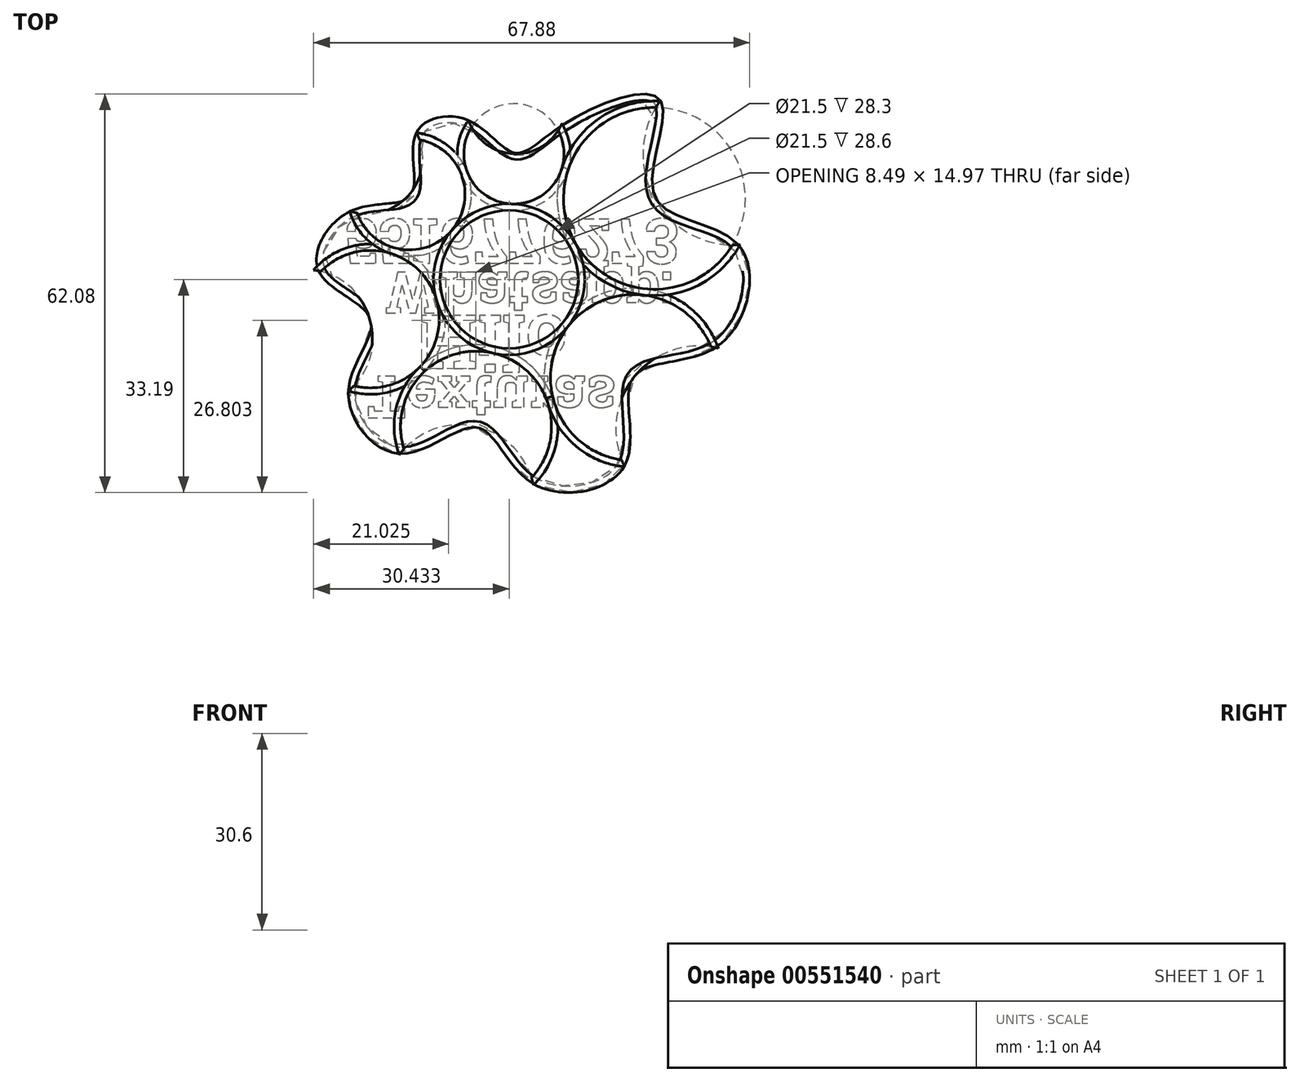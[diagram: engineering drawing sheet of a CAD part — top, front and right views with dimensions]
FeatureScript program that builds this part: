
annotation { "Feature Type Name" : "Feature", "Feature Type Description" : "" }
export const myFeature = defineFeature(function(context is Context, id is Id, definition is map)
    precondition{}
    {
        {
            var Q0;
            Q0=qCreatedBy(makeId("Top.planeOp"),FACE);
            var sketch = newSketch(context, id + "F0", { "sketchPlane" : qUnion([Q0])});
            skCircle(sketch, "E0", {"center": v(0, 0) * mm, "radius": 10.75 * mm});
            skCircle(sketch, "E1", {"center": v(14.53, -21.44) * mm, "radius": 14.15 * mm});
            skCircle(sketch, "E2", {"center": v(-13.56, -20.65) * mm, "radius": 12.95 * mm});
            skCircle(sketch, "E3", {"center": v(-23.3, 3.14) * mm, "radius": 11.75 * mm});
            skCircle(sketch, "E4", {"center": v(-8.05, 20.96) * mm, "radius": 10.7 * mm});
            skCircle(sketch, "E5", {"center": v(11.83, 16.62) * mm, "radius": 8.65 * mm});
            skCircle(sketch, "E6", {"center": v(19.53, 0.96) * mm, "radius": 7.8 * mm});
            skCircle(sketch, "E7", {"center": v(0, 0) * mm, "radius": 19.4 * mm});
            skLineSegment(sketch, "E8", {"start": v(0, 0) * mm, "end": v(14.53, -21.44) * mm, "construction": true});
            skLineSegment(sketch, "E9", {"start": v(0, 0) * mm, "end": v(19.53, 0.96) * mm, "construction": true});
            skLineSegment(sketch, "E10", {"start": v(0, 0) * mm, "end": v(11.83, 16.62) * mm, "construction": true});
            skLineSegment(sketch, "E11", {"start": v(0, 0) * mm, "end": v(-8.05, 20.96) * mm, "construction": true});
            skLineSegment(sketch, "E12", {"start": v(0, 0) * mm, "end": v(-23.3, 3.14) * mm, "construction": true});
            skLineSegment(sketch, "E13", {"start": v(0, 0) * mm, "end": v(-13.56, -20.65) * mm, "construction": true});
            skLineSegment(sketch, "E14", {"start": v(-13.56, -20.65) * mm, "end": v(-26.3, -40.07) * mm, "construction": true});
            skLineSegment(sketch, "E15", {"start": v(14.53, -21.44) * mm, "end": v(30.4, -44.87) * mm, "construction": true});
            skLineSegment(sketch, "E16", {"start": v(19.53, 0.96) * mm, "end": v(43.85, 2.15) * mm, "construction": true});
            skLineSegment(sketch, "E17", {"start": v(11.83, 16.62) * mm, "end": v(22.56, 31.7) * mm, "construction": true});
            skLineSegment(sketch, "E18", {"start": v(-8.05, 20.96) * mm, "end": v(-13.82, 35.98) * mm, "construction": true});
            skLineSegment(sketch, "E19", {"start": v(-23.3, 3.14) * mm, "end": v(-53.03, 7.14) * mm, "construction": true});
            skCircle(sketch, "E20", {"center": v(27.32, 1.34) * mm, "radius": 7.8 * mm});
            skCircle(sketch, "E21", {"center": v(16.85, 23.67) * mm, "radius": 8.65 * mm});
            skCircle(sketch, "E22", {"center": v(-11.89, 30.95) * mm, "radius": 10.7 * mm});
            skCircle(sketch, "E23", {"center": v(-34.94, 4.7) * mm, "radius": 11.75 * mm});
            skCircle(sketch, "E24", {"center": v(-20.66, -31.47) * mm, "radius": 12.95 * mm});
            skCircle(sketch, "E25", {"center": v(22.47, -33.15) * mm, "radius": 14.15 * mm});
            skSolve(sketch);
        }
        {
            var Q0;
            {var subQ0=sQuery(id+"F0.wireOp",EDGE,"E7");var subQ1=sQuery(id+"F0.wireOp",EDGE,"E6");var subQ2=makeQuery(id+"F0.imprint","INTERSECT",VERTEX,{"disambiguationData":[OD(0.0)],"derivedFrom":[subQ1,subQ0]});Q0=makeQuery(id+"F0.imprint","IMPRINT",FACE,{"disambiguationData":[TD([[makeQuery(id+"F0.imprint","IMPRINT",EDGE,{"disambiguationData":[TD([[subQ2,-1.0]])],"derivedFrom":subQ1}),1.0]])]});}
            var Q1;
            {var subQ0=sQuery(id+"F0.wireOp",EDGE,"E7");var subQ1=sQuery(id+"F0.wireOp",EDGE,"E6");var subQ2=makeQuery(id+"F0.imprint","INTERSECT",VERTEX,{"disambiguationData":[OD(0.0)],"derivedFrom":[subQ1,subQ0]});Q1=makeQuery(id+"F0.imprint","IMPRINT",FACE,{"disambiguationData":[TD([[makeQuery(id+"F0.imprint","IMPRINT",EDGE,{"disambiguationData":[TD([[subQ2,1.0]])],"derivedFrom":subQ1}),1.0]])]});}
            extrude(context, id + "F1", {"entities" : qUnion([Q0, Q1]), "depth" : 19 * mm, "offsetDistance" : 25 * mm});
        }
        {
            var Q0;
            Q0=makeQuery(id+"F0.imprint","IMPRINT",FACE,{"disambiguationData":[TD([[makeQuery(id+"F0.imprint","IMPRINT",EDGE,{"derivedFrom":sQuery(id+"F0.wireOp",EDGE,"E5")}),1.0]])]});
            var Q1;
            {var subQ0=sQuery(id+"F0.wireOp",EDGE,"E7");var subQ1=sQuery(id+"F0.wireOp",EDGE,"E5");var subQ2=makeQuery(id+"F0.imprint","INTERSECT",VERTEX,{"disambiguationData":[OD(0.0)],"derivedFrom":[subQ1,subQ0]});Q1=makeQuery(id+"F0.imprint","IMPRINT",FACE,{"disambiguationData":[TD([[makeQuery(id+"F0.imprint","IMPRINT",EDGE,{"disambiguationData":[TD([[subQ2,-1.0]])],"derivedFrom":subQ1}),1.0]])]});}
            var Q2;
            {var subQ0=sQuery(id+"F0.wireOp",EDGE,"E21");var subQ1=sQuery(id+"F0.wireOp",EDGE,"E5");var subQ2=makeQuery(id+"F0.imprint","INTERSECT",VERTEX,{"disambiguationData":[OD(0.0)],"derivedFrom":[subQ1,subQ0]});Q2=makeQuery(id+"F0.imprint","IMPRINT",FACE,{"disambiguationData":[TD([[makeQuery(id+"F0.imprint","IMPRINT",EDGE,{"disambiguationData":[TD([[subQ2,1.0]])],"derivedFrom":subQ1}),1.0]])]});}
            extrude(context, id + "F2", {"entities" : qUnion([Q0, Q1, Q2]), "depth" : 20.9 * mm, "offsetDistance" : 25 * mm});
        }
        {
            var Q0;
            Q0=makeQuery(id+"F0.imprint","IMPRINT",FACE,{"disambiguationData":[TD([[makeQuery(id+"F0.imprint","IMPRINT",EDGE,{"derivedFrom":sQuery(id+"F0.wireOp",EDGE,"E4")}),1.0]])]});
            var Q1;
            {var subQ0=sQuery(id+"F0.wireOp",EDGE,"E7");var subQ1=sQuery(id+"F0.wireOp",EDGE,"E4");var subQ2=makeQuery(id+"F0.imprint","INTERSECT",VERTEX,{"disambiguationData":[OD(0.0)],"derivedFrom":[subQ1,subQ0]});Q1=makeQuery(id+"F0.imprint","IMPRINT",FACE,{"disambiguationData":[TD([[makeQuery(id+"F0.imprint","IMPRINT",EDGE,{"disambiguationData":[TD([[subQ2,-1.0]])],"derivedFrom":subQ1}),1.0]])]});}
            var Q2;
            {var subQ0=sQuery(id+"F0.wireOp",EDGE,"E22");var subQ1=sQuery(id+"F0.wireOp",EDGE,"E4");var subQ2=makeQuery(id+"F0.imprint","INTERSECT",VERTEX,{"disambiguationData":[OD(0.0)],"derivedFrom":[subQ1,subQ0]});Q2=makeQuery(id+"F0.imprint","IMPRINT",FACE,{"disambiguationData":[TD([[makeQuery(id+"F0.imprint","IMPRINT",EDGE,{"disambiguationData":[TD([[subQ2,1.0]])],"derivedFrom":subQ1}),1.0]])]});}
            extrude(context, id + "F3", {"entities" : qUnion([Q0, Q1, Q2]), "depth" : 16.1 * mm, "offsetDistance" : 25 * mm});
        }
        {
            var Q0;
            Q0=makeQuery(id+"F0.imprint","IMPRINT",FACE,{"disambiguationData":[TD([[makeQuery(id+"F0.imprint","IMPRINT",EDGE,{"derivedFrom":sQuery(id+"F0.wireOp",EDGE,"E3")}),1.0]])]});
            var Q1;
            {var subQ0=sQuery(id+"F0.wireOp",EDGE,"E7");var subQ1=sQuery(id+"F0.wireOp",EDGE,"E3");var subQ2=makeQuery(id+"F0.imprint","INTERSECT",VERTEX,{"disambiguationData":[OD(0.0)],"derivedFrom":[subQ1,subQ0]});Q1=makeQuery(id+"F0.imprint","IMPRINT",FACE,{"disambiguationData":[TD([[makeQuery(id+"F0.imprint","IMPRINT",EDGE,{"disambiguationData":[TD([[subQ2,1.0]])],"derivedFrom":subQ1}),1.0]])]});}
            var Q2;
            {var subQ0=sQuery(id+"F0.wireOp",EDGE,"E23");var subQ1=sQuery(id+"F0.wireOp",EDGE,"E3");var subQ2=makeQuery(id+"F0.imprint","INTERSECT",VERTEX,{"disambiguationData":[OD(0.0)],"derivedFrom":[subQ1,subQ0]});Q2=makeQuery(id+"F0.imprint","IMPRINT",FACE,{"disambiguationData":[TD([[makeQuery(id+"F0.imprint","IMPRINT",EDGE,{"disambiguationData":[TD([[subQ2,-1.0]])],"derivedFrom":subQ1}),1.0]])]});}
            extrude(context, id + "F4", {"entities" : qUnion([Q0, Q1, Q2]), "depth" : 17.1 * mm, "offsetDistance" : 25 * mm});
        }
        {
            var Q0;
            Q0=makeQuery(id+"F0.imprint","IMPRINT",FACE,{"disambiguationData":[TD([[makeQuery(id+"F0.imprint","IMPRINT",EDGE,{"derivedFrom":sQuery(id+"F0.wireOp",EDGE,"E2")}),1.0]])]});
            var Q1;
            {var subQ0=sQuery(id+"F0.wireOp",EDGE,"E7");var subQ1=sQuery(id+"F0.wireOp",EDGE,"E2");var subQ2=makeQuery(id+"F0.imprint","INTERSECT",VERTEX,{"disambiguationData":[OD(0.0)],"derivedFrom":[subQ1,subQ0]});Q1=makeQuery(id+"F0.imprint","IMPRINT",FACE,{"disambiguationData":[TD([[makeQuery(id+"F0.imprint","IMPRINT",EDGE,{"disambiguationData":[TD([[subQ2,1.0]])],"derivedFrom":subQ1}),1.0]])]});}
            var Q2;
            {var subQ0=sQuery(id+"F0.wireOp",EDGE,"E24");var subQ1=sQuery(id+"F0.wireOp",EDGE,"E2");var subQ2=makeQuery(id+"F0.imprint","INTERSECT",VERTEX,{"disambiguationData":[OD(0.0)],"derivedFrom":[subQ1,subQ0]});Q2=makeQuery(id+"F0.imprint","IMPRINT",FACE,{"disambiguationData":[TD([[makeQuery(id+"F0.imprint","IMPRINT",EDGE,{"disambiguationData":[TD([[subQ2,-1.0]])],"derivedFrom":subQ1}),1.0]])]});}
            extrude(context, id + "F5", {"entities" : qUnion([Q0, Q1, Q2]), "depth" : 18.9 * mm, "offsetDistance" : 25 * mm});
        }
        {
            var Q0;
            Q0=makeQuery(id+"F0.imprint","IMPRINT",FACE,{"disambiguationData":[TD([[makeQuery(id+"F0.imprint","IMPRINT",EDGE,{"derivedFrom":sQuery(id+"F0.wireOp",EDGE,"E1")}),1.0]])]});
            var Q1;
            {var subQ0=sQuery(id+"F0.wireOp",EDGE,"E7");var subQ1=sQuery(id+"F0.wireOp",EDGE,"E1");var subQ2=makeQuery(id+"F0.imprint","INTERSECT",VERTEX,{"disambiguationData":[OD(0.0)],"derivedFrom":[subQ1,subQ0]});Q1=makeQuery(id+"F0.imprint","IMPRINT",FACE,{"disambiguationData":[TD([[makeQuery(id+"F0.imprint","IMPRINT",EDGE,{"disambiguationData":[TD([[subQ2,-1.0]])],"derivedFrom":subQ1}),1.0]])]});}
            var Q2;
            {var subQ0=sQuery(id+"F0.wireOp",EDGE,"E25");var subQ1=sQuery(id+"F0.wireOp",EDGE,"E1");var subQ2=makeQuery(id+"F0.imprint","INTERSECT",VERTEX,{"disambiguationData":[OD(0.0)],"derivedFrom":[subQ1,subQ0]});Q2=makeQuery(id+"F0.imprint","IMPRINT",FACE,{"disambiguationData":[TD([[makeQuery(id+"F0.imprint","IMPRINT",EDGE,{"disambiguationData":[TD([[subQ2,1.0]])],"derivedFrom":subQ1}),1.0]])]});}
            extrude(context, id + "F6", {"entities" : qUnion([Q0, Q1, Q2]), "depth" : 22 * mm, "offsetDistance" : 25 * mm});
        }
        {
            var Q0;
            Q0=makeQuery(id+"F3.opExtrude","CAP_FACE",FACE,{"disambiguationData":[OSD([sQuery(id+"F0.wireOp",EDGE,"E4")])],"isStart":false});
            var Q1;
            Q1=makeQuery(id+"F4.opExtrude","CAP_FACE",FACE,{"disambiguationData":[OSD([sQuery(id+"F0.wireOp",EDGE,"E3")])],"isStart":false});
            var Q2;
            Q2=makeQuery(id+"F5.opExtrude","CAP_FACE",FACE,{"disambiguationData":[OSD([sQuery(id+"F0.wireOp",EDGE,"E2")])],"isStart":false});
            var Q3;
            Q3=makeQuery(id+"F6.opExtrude","CAP_FACE",FACE,{"disambiguationData":[OSD([sQuery(id+"F0.wireOp",EDGE,"E1")])],"isStart":false});
            var Q4;
            Q4=makeQuery(id+"F1.opExtrude","CAP_FACE",FACE,{"disambiguationData":[OSD([sQuery(id+"F0.wireOp",EDGE,"E6")])],"isStart":false});
            var Q5;
            Q5=makeQuery(id+"F2.opExtrude","CAP_FACE",FACE,{"disambiguationData":[OSD([sQuery(id+"F0.wireOp",EDGE,"E5")])],"isStart":false});
            shell(context, id + "F7", {"entities" : qUnion([Q0, Q1, Q2, Q3, Q4, Q5]), "thickness" : 1 * mm, "oppositeDirection" : true});
        }
        {
            var Q0;
            Q0=makeQuery(id+"F0.imprint","IMPRINT",FACE,{"disambiguationData":[TD([[makeQuery(id+"F0.imprint","IMPRINT",EDGE,{"derivedFrom":sQuery(id+"F0.wireOp",EDGE,"E0")}),-1.0]])]});
            extrude(context, id + "F8", {"entities" : qUnion([Q0]), "depth" : 28.3 * mm, "offsetDistance" : 25 * mm});
        }
        {
            var Q0;
            Q0=makeQuery(id+"F0.imprint","IMPRINT",FACE,{"disambiguationData":[TD([[makeQuery(id+"F0.imprint","IMPRINT",EDGE,{"derivedFrom":sQuery(id+"F0.wireOp",EDGE,"E0")}),1.0]])]});
            extrude(context, id + "F9", {"entities" : qUnion([Q0]), "depth" : 28.6 * mm, "offsetDistance" : 25 * mm});
        }
        {
            var Q0;
            Q0=makeQuery(id+"F9.opExtrude","CAP_FACE",FACE,{"disambiguationData":[OSD([sQuery(id+"F0.wireOp",EDGE,"E0")])],"isStart":false});
            shell(context, id + "F10", {"entities" : qUnion([Q0]), "thickness" : 1 * mm, "oppositeDirection" : true});
        }
        {
            var Q0;
            {var subQ0=sQuery(id+"F0.wireOp",EDGE,"E7");Q0=makeQuery(id+"F8.opExtrude","CAP_EDGE",EDGE,{"disambiguationData":[OSD([subQ0]),TDD([makeQuery(id+"F0.imprint","IMPRINT",EDGE,{"disambiguationData":[TD([[makeQuery(id+"F0.imprint","INTERSECT",VERTEX,{"disambiguationData":[OD(0.0)],"derivedFrom":[sQuery(id+"F0.wireOp",EDGE,"E5"),subQ0]}),1.0]])],"derivedFrom":subQ0})])],"isStart":false});}
            var Q1;
            {var subQ0=sQuery(id+"F0.wireOp",EDGE,"E7");Q1=makeQuery(id+"F8.opExtrude","CAP_EDGE",EDGE,{"disambiguationData":[OSD([subQ0]),TDD([makeQuery(id+"F0.imprint","IMPRINT",EDGE,{"disambiguationData":[TD([[makeQuery(id+"F0.imprint","INTERSECT",VERTEX,{"disambiguationData":[OD(0.0)],"derivedFrom":[sQuery(id+"F0.wireOp",EDGE,"E4"),subQ0]}),1.0]])],"derivedFrom":subQ0})])],"isStart":false});}
            var Q2;
            {var subQ0=sQuery(id+"F0.wireOp",EDGE,"E7");Q2=makeQuery(id+"F8.opExtrude","CAP_EDGE",EDGE,{"disambiguationData":[OSD([subQ0]),TDD([makeQuery(id+"F0.imprint","IMPRINT",EDGE,{"disambiguationData":[TD([[makeQuery(id+"F0.imprint","INTERSECT",VERTEX,{"disambiguationData":[OD(1.0)],"derivedFrom":[sQuery(id+"F0.wireOp",EDGE,"E1"),subQ0]}),-1.0]])],"derivedFrom":subQ0})])],"isStart":false});}
            var Q3;
            {var subQ0=sQuery(id+"F0.wireOp",EDGE,"E7");Q3=makeQuery(id+"F8.opExtrude","CAP_EDGE",EDGE,{"disambiguationData":[OSD([subQ0]),TDD([makeQuery(id+"F0.imprint","IMPRINT",EDGE,{"disambiguationData":[TD([[makeQuery(id+"F0.imprint","INTERSECT",VERTEX,{"disambiguationData":[OD(0.0)],"derivedFrom":[sQuery(id+"F0.wireOp",EDGE,"E1"),subQ0]}),1.0]])],"derivedFrom":subQ0})])],"isStart":false});}
            var Q4;
            {var subQ0=sQuery(id+"F0.wireOp",EDGE,"E7");Q4=makeQuery(id+"F8.opExtrude","CAP_EDGE",EDGE,{"disambiguationData":[OSD([subQ0]),TDD([makeQuery(id+"F0.imprint","IMPRINT",EDGE,{"disambiguationData":[TD([[makeQuery(id+"F0.imprint","INTERSECT",VERTEX,{"disambiguationData":[OD(0.0)],"derivedFrom":[sQuery(id+"F0.wireOp",EDGE,"E3"),subQ0]}),1.0]])],"derivedFrom":subQ0})])],"isStart":false});}
            var Q5;
            {var subQ0=sQuery(id+"F0.wireOp",EDGE,"E7");Q5=makeQuery(id+"F8.opExtrude","CAP_EDGE",EDGE,{"disambiguationData":[OSD([subQ0]),TDD([makeQuery(id+"F0.imprint","IMPRINT",EDGE,{"disambiguationData":[TD([[makeQuery(id+"F0.imprint","INTERSECT",VERTEX,{"disambiguationData":[OD(0.0)],"derivedFrom":[sQuery(id+"F0.wireOp",EDGE,"E2"),subQ0]}),1.0]])],"derivedFrom":subQ0})])],"isStart":false});}
            var Q6;
            {var subQ0=sQuery(id+"F0.wireOp",EDGE,"E7");Q6=makeQuery(id+"F8.opExtrude","CAP_EDGE",EDGE,{"disambiguationData":[OSD([subQ0]),TDD([makeQuery(id+"F0.imprint","IMPRINT",EDGE,{"disambiguationData":[TD([[makeQuery(id+"F0.imprint","INTERSECT",VERTEX,{"disambiguationData":[OD(1.0)],"derivedFrom":[sQuery(id+"F0.wireOp",EDGE,"E1"),subQ0]}),1.0]])],"derivedFrom":subQ0})])],"isStart":false});}
            var Q7;
            {var subQ0=sQuery(id+"F0.wireOp",EDGE,"E7");Q7=makeQuery(id+"F8.opExtrude","CAP_EDGE",EDGE,{"disambiguationData":[OSD([subQ0]),TDD([makeQuery(id+"F0.imprint","IMPRINT",EDGE,{"disambiguationData":[TD([[makeQuery(id+"F0.imprint","INTERSECT",VERTEX,{"disambiguationData":[OD(0.0)],"derivedFrom":[sQuery(id+"F0.wireOp",EDGE,"E1"),subQ0]}),-1.0]])],"derivedFrom":subQ0})])],"isStart":false});}
            var Q8;
            {var subQ0=sQuery(id+"F0.wireOp",EDGE,"E7");Q8=makeQuery(id+"F8.opExtrude","CAP_EDGE",EDGE,{"disambiguationData":[OSD([subQ0]),TDD([makeQuery(id+"F0.imprint","IMPRINT",EDGE,{"disambiguationData":[TD([[makeQuery(id+"F0.imprint","INTERSECT",VERTEX,{"disambiguationData":[OD(1.0)],"derivedFrom":[sQuery(id+"F0.wireOp",EDGE,"E5"),subQ0]}),1.0]])],"derivedFrom":subQ0})])],"isStart":false});}
            var Q9;
            {var subQ0=sQuery(id+"F0.wireOp",EDGE,"E7");Q9=makeQuery(id+"F8.opExtrude","CAP_EDGE",EDGE,{"disambiguationData":[OSD([subQ0]),TDD([makeQuery(id+"F0.imprint","IMPRINT",EDGE,{"disambiguationData":[TD([[makeQuery(id+"F0.imprint","INTERSECT",VERTEX,{"disambiguationData":[OD(1.0)],"derivedFrom":[sQuery(id+"F0.wireOp",EDGE,"E4"),subQ0]}),1.0]])],"derivedFrom":subQ0})])],"isStart":false});}
            fillet(context, id + "F11", {"entities" : qUnion([Q0, Q1, Q2, Q3, Q4, Q5, Q6, Q7, Q8, Q9]), "radius" : 7.5 * mm, "tangentPropagation" : true, "allowEdgeOverflow" : false});
        }
        {
            var Q0;
            {var subQ0=sQuery(id+"F0.wireOp",EDGE,"E21");var subQ1=sQuery(id+"F0.wireOp",EDGE,"E5");var subQ2=makeQuery(id+"F0.imprint","INTERSECT",VERTEX,{"disambiguationData":[OD(0.0)],"derivedFrom":[subQ1,subQ0]});Q0=makeQuery(id+"F0.imprint","IMPRINT",FACE,{"disambiguationData":[TD([[makeQuery(id+"F0.imprint","IMPRINT",EDGE,{"disambiguationData":[TD([[subQ2,1.0]])],"derivedFrom":subQ1}),1.0]])]});}
            var Q1;
            {var subQ0=sQuery(id+"F0.wireOp",EDGE,"E21");var subQ1=sQuery(id+"F0.wireOp",EDGE,"E5");var subQ2=makeQuery(id+"F0.imprint","INTERSECT",VERTEX,{"disambiguationData":[OD(0.0)],"derivedFrom":[subQ1,subQ0]});Q1=makeQuery(id+"F0.imprint","IMPRINT",FACE,{"disambiguationData":[TD([[makeQuery(id+"F0.imprint","IMPRINT",EDGE,{"disambiguationData":[TD([[subQ2,1.0]])],"derivedFrom":subQ1}),-1.0]])]});}
            extrude(context, id + "F12", {"entities" : qUnion([Q0, Q1]), "operationType" : NewBodyOperationType.REMOVE, "endBound" : BoundingType.SYMMETRIC, "depth" : 56.4 * mm, "offsetDistance" : 25 * mm});
        }
        {
            var Q0;
            {var subQ0=sQuery(id+"F0.wireOp",EDGE,"E22");var subQ1=sQuery(id+"F0.wireOp",EDGE,"E4");var subQ2=makeQuery(id+"F0.imprint","INTERSECT",VERTEX,{"disambiguationData":[OD(0.0)],"derivedFrom":[subQ1,subQ0]});Q0=makeQuery(id+"F0.imprint","IMPRINT",FACE,{"disambiguationData":[TD([[makeQuery(id+"F0.imprint","IMPRINT",EDGE,{"disambiguationData":[TD([[subQ2,1.0]])],"derivedFrom":subQ1}),-1.0]])]});}
            var Q1;
            {var subQ0=sQuery(id+"F0.wireOp",EDGE,"E22");var subQ1=sQuery(id+"F0.wireOp",EDGE,"E4");var subQ2=makeQuery(id+"F0.imprint","INTERSECT",VERTEX,{"disambiguationData":[OD(0.0)],"derivedFrom":[subQ1,subQ0]});Q1=makeQuery(id+"F0.imprint","IMPRINT",FACE,{"disambiguationData":[TD([[makeQuery(id+"F0.imprint","IMPRINT",EDGE,{"disambiguationData":[TD([[subQ2,1.0]])],"derivedFrom":subQ1}),1.0]])]});}
            extrude(context, id + "F13", {"entities" : qUnion([Q0, Q1]), "operationType" : NewBodyOperationType.REMOVE, "endBound" : BoundingType.SYMMETRIC, "depth" : 44.6 * mm, "offsetDistance" : 25 * mm});
        }
        {
            var Q0;
            {var subQ0=sQuery(id+"F0.wireOp",EDGE,"E23");var subQ1=sQuery(id+"F0.wireOp",EDGE,"E3");var subQ2=makeQuery(id+"F0.imprint","INTERSECT",VERTEX,{"disambiguationData":[OD(0.0)],"derivedFrom":[subQ1,subQ0]});Q0=makeQuery(id+"F0.imprint","IMPRINT",FACE,{"disambiguationData":[TD([[makeQuery(id+"F0.imprint","IMPRINT",EDGE,{"disambiguationData":[TD([[subQ2,-1.0]])],"derivedFrom":subQ1}),1.0]])]});}
            var Q1;
            {var subQ0=sQuery(id+"F0.wireOp",EDGE,"E23");var subQ1=sQuery(id+"F0.wireOp",EDGE,"E3");var subQ2=makeQuery(id+"F0.imprint","INTERSECT",VERTEX,{"disambiguationData":[OD(0.0)],"derivedFrom":[subQ1,subQ0]});Q1=makeQuery(id+"F0.imprint","IMPRINT",FACE,{"disambiguationData":[TD([[makeQuery(id+"F0.imprint","IMPRINT",EDGE,{"disambiguationData":[TD([[subQ2,-1.0]])],"derivedFrom":subQ1}),-1.0]])]});}
            extrude(context, id + "F14", {"entities" : qUnion([Q0, Q1]), "operationType" : NewBodyOperationType.REMOVE, "endBound" : BoundingType.SYMMETRIC, "depth" : 38.6 * mm, "offsetDistance" : 25 * mm});
        }
        {
            var Q0;
            {var subQ0=sQuery(id+"F0.wireOp",EDGE,"E24");var subQ1=sQuery(id+"F0.wireOp",EDGE,"E2");var subQ2=makeQuery(id+"F0.imprint","INTERSECT",VERTEX,{"disambiguationData":[OD(0.0)],"derivedFrom":[subQ1,subQ0]});Q0=makeQuery(id+"F0.imprint","IMPRINT",FACE,{"disambiguationData":[TD([[makeQuery(id+"F0.imprint","IMPRINT",EDGE,{"disambiguationData":[TD([[subQ2,-1.0]])],"derivedFrom":subQ1}),1.0]])]});}
            var Q1;
            {var subQ0=sQuery(id+"F0.wireOp",EDGE,"E24");var subQ1=sQuery(id+"F0.wireOp",EDGE,"E2");var subQ2=makeQuery(id+"F0.imprint","INTERSECT",VERTEX,{"disambiguationData":[OD(0.0)],"derivedFrom":[subQ1,subQ0]});Q1=makeQuery(id+"F0.imprint","IMPRINT",FACE,{"disambiguationData":[TD([[makeQuery(id+"F0.imprint","IMPRINT",EDGE,{"disambiguationData":[TD([[subQ2,-1.0]])],"derivedFrom":subQ1}),-1.0]])]});}
            extrude(context, id + "F15", {"entities" : qUnion([Q0, Q1]), "operationType" : NewBodyOperationType.REMOVE, "endBound" : BoundingType.SYMMETRIC, "depth" : 46.2 * mm, "offsetDistance" : 25 * mm});
        }
        {
            var Q0;
            {var subQ0=sQuery(id+"F0.wireOp",EDGE,"E25");var subQ1=sQuery(id+"F0.wireOp",EDGE,"E1");var subQ2=makeQuery(id+"F0.imprint","INTERSECT",VERTEX,{"disambiguationData":[OD(0.0)],"derivedFrom":[subQ1,subQ0]});Q0=makeQuery(id+"F0.imprint","IMPRINT",FACE,{"disambiguationData":[TD([[makeQuery(id+"F0.imprint","IMPRINT",EDGE,{"disambiguationData":[TD([[subQ2,1.0]])],"derivedFrom":subQ1}),1.0]])]});}
            var Q1;
            {var subQ0=sQuery(id+"F0.wireOp",EDGE,"E25");var subQ1=sQuery(id+"F0.wireOp",EDGE,"E1");var subQ2=makeQuery(id+"F0.imprint","INTERSECT",VERTEX,{"disambiguationData":[OD(0.0)],"derivedFrom":[subQ1,subQ0]});Q1=makeQuery(id+"F0.imprint","IMPRINT",FACE,{"disambiguationData":[TD([[makeQuery(id+"F0.imprint","IMPRINT",EDGE,{"disambiguationData":[TD([[subQ2,1.0]])],"derivedFrom":subQ1}),-1.0]])]});}
            extrude(context, id + "F16", {"entities" : qUnion([Q0, Q1]), "operationType" : NewBodyOperationType.REMOVE, "endBound" : BoundingType.SYMMETRIC, "depth" : 47.6 * mm, "offsetDistance" : 25 * mm});
        }
        {
            var Q0;
            {var subQ0=sQuery(id+"F0.wireOp",EDGE,"E20");var subQ1=sQuery(id+"F0.wireOp",EDGE,"E6");var subQ2=makeQuery(id+"F0.imprint","INTERSECT",VERTEX,{"disambiguationData":[OD(0.0)],"derivedFrom":[subQ1,subQ0]});Q0=makeQuery(id+"F0.imprint","IMPRINT",FACE,{"disambiguationData":[TD([[makeQuery(id+"F0.imprint","IMPRINT",EDGE,{"disambiguationData":[TD([[subQ2,1.0]])],"derivedFrom":subQ1}),1.0]])]});}
            var Q1;
            {var subQ0=sQuery(id+"F0.wireOp",EDGE,"E20");var subQ1=sQuery(id+"F0.wireOp",EDGE,"E6");var subQ2=makeQuery(id+"F0.imprint","INTERSECT",VERTEX,{"disambiguationData":[OD(0.0)],"derivedFrom":[subQ1,subQ0]});Q1=makeQuery(id+"F0.imprint","IMPRINT",FACE,{"disambiguationData":[TD([[makeQuery(id+"F0.imprint","IMPRINT",EDGE,{"disambiguationData":[TD([[subQ2,1.0]])],"derivedFrom":subQ1}),-1.0]])]});}
            extrude(context, id + "F17", {"entities" : qUnion([Q0, Q1]), "operationType" : NewBodyOperationType.REMOVE, "endBound" : BoundingType.SYMMETRIC, "depth" : 47.8 * mm, "offsetDistance" : 25 * mm});
        }
        {
            var Q0;
            Q0=makeQuery(id+"F3.opExtrude","CAP_FACE",FACE,{"disambiguationData":[OSD([sQuery(id+"F0.wireOp",EDGE,"E4")])],"isStart":true});
            var sketch = newSketch(context, id + "F18", { "sketchPlane" : qUnion([Q0])});
            skFitSpline(sketch, "E26", {"points": [v(-28.5, -14.4) * mm, v(-19.49, -23.42) * mm, v(-8.05, -20.96) * mm, v(-1.27, -29.64) * mm, v(8.57, -25.27) * mm, v(11.7, -16.35) * mm, v(21.35, -16.41) * mm, v(24.15, -8.65) * mm, v(19.7, -0.93) * mm, v(24.63, 6.17) * mm, v(29.86, 20.97) * mm, v(14.77, 21.5) * mm, v(8.37, 35.2) * mm, v(-7.42, 33.33) * mm, v(-13.46, 20.54) * mm, v(-27.26, 20.45) * mm, v(-31.4, 6.6) * mm, v(-23.43, -2.94) * mm, v(-28.5, -14.4) * mm]});
            skArc(sketch, "E27.trimOffspring", {"start": v(-7.38, -21.37) * mm, "mid": v(-8.24, -21.01) * mm, "end": v(-9.12, -20.73) * mm});
            skSolve(sketch);
        }
        {
            var Q0;
            {var subQ0=sQuery(id+"F0.wireOp",EDGE,"E2");Q0=makeQuery(id+"F15.boolean.opBoolean","INTERSECT",EDGE,{"derivedFrom":[makeQuery(id+"F7.opShell","OFFSET_FACE",FACE,{"disambiguationData":[OSD([subQ0]),TDD([makeQuery(id+"F5.opExtrude","CAP_FACE",FACE,{"disambiguationData":[OSD([subQ0])],"isStart":true})])]}),makeQuery(id+"F15.opExtrude","SWEPT_FACE",FACE,{"disambiguationData":[OSD([sQuery(id+"F0.wireOp",EDGE,"E24")])]})]});}
            var Q1;
            {var subQ0=sQuery(id+"F0.wireOp",EDGE,"E1");Q1=makeQuery(id+"F16.boolean.opBoolean","INTERSECT",EDGE,{"derivedFrom":[makeQuery(id+"F7.opShell","OFFSET_FACE",FACE,{"disambiguationData":[OSD([subQ0]),TDD([makeQuery(id+"F6.opExtrude","CAP_FACE",FACE,{"disambiguationData":[OSD([subQ0])],"isStart":true})])]}),makeQuery(id+"F16.opExtrude","SWEPT_FACE",FACE,{"disambiguationData":[OSD([sQuery(id+"F0.wireOp",EDGE,"E25")])]})]});}
            var Q2;
            {var subQ0=sQuery(id+"F0.wireOp",EDGE,"E3");Q2=makeQuery(id+"F14.boolean.opBoolean","INTERSECT",EDGE,{"derivedFrom":[makeQuery(id+"F7.opShell","OFFSET_FACE",FACE,{"disambiguationData":[OSD([subQ0]),TDD([makeQuery(id+"F4.opExtrude","CAP_FACE",FACE,{"disambiguationData":[OSD([subQ0])],"isStart":true})])]}),makeQuery(id+"F14.opExtrude","SWEPT_FACE",FACE,{"disambiguationData":[OSD([sQuery(id+"F0.wireOp",EDGE,"E23")])]})]});}
            var Q3;
            {var subQ0=sQuery(id+"F0.wireOp",EDGE,"E4");Q3=makeQuery(id+"F13.boolean.opBoolean","INTERSECT",EDGE,{"derivedFrom":[makeQuery(id+"F7.opShell","OFFSET_FACE",FACE,{"disambiguationData":[OSD([subQ0]),TDD([makeQuery(id+"F3.opExtrude","CAP_FACE",FACE,{"disambiguationData":[OSD([subQ0])],"isStart":true})])]}),makeQuery(id+"F13.opExtrude","SWEPT_FACE",FACE,{"disambiguationData":[OSD([sQuery(id+"F0.wireOp",EDGE,"E22")])]})]});}
            var Q4;
            {var subQ0=sQuery(id+"F0.wireOp",EDGE,"E5");Q4=makeQuery(id+"F12.boolean.opBoolean","INTERSECT",EDGE,{"derivedFrom":[makeQuery(id+"F7.opShell","OFFSET_FACE",FACE,{"disambiguationData":[OSD([subQ0]),TDD([makeQuery(id+"F2.opExtrude","CAP_FACE",FACE,{"disambiguationData":[OSD([subQ0])],"isStart":true})])]}),makeQuery(id+"F12.opExtrude","SWEPT_FACE",FACE,{"disambiguationData":[OSD([sQuery(id+"F0.wireOp",EDGE,"E21")])]})]});}
            var Q5;
            {var subQ0=sQuery(id+"F0.wireOp",EDGE,"E20");Q5=makeQuery(id+"F7.opShell","OFFSET_EDGE",EDGE,{"disambiguationData":[OSD([subQ0]),TDD([makeQuery(id+"F1.opExtrude","CAP_EDGE",EDGE,{"disambiguationData":[OSD([subQ0])],"isStart":true})])]});}
            fillet(context, id + "F19", {"entities" : qUnion([Q0, Q1, Q2, Q3, Q4, Q5]), "radius" : 1 * mm, "tangentPropagation" : true, "allowEdgeOverflow" : false});
        }
        {
            var Q0;
            Q0 = qSketchRegion(id + "F18", true);
            extrude(context, id + "F20", {"entities" : qUnion([Q0]), "depth" : -1 * mm, "offsetDistance" : 25 * mm});
        }
        {
            var Q0;
            Q0=makeQuery(id+"F20.opExtrude","CAP_EDGE",EDGE,{"disambiguationData":[OSD([sQuery(id+"F18.wireOp",EDGE,"E26")])],"isStart":false});
            fillet(context, id + "F21", {"entities" : qUnion([Q0]), "radius" : 1 * mm, "tangentPropagation" : true, "allowEdgeOverflow" : false});
        }
        {
            var Q0;
            Q0 = qSketchRegion(id + "F18", true);
            extrude(context, id + "F22", {"entities" : qUnion([Q0]), "depth" : 1 * mm, "offsetDistance" : 25 * mm});
        }
        {
            var Q0;
            Q0=makeQuery(id+"F22.opExtrude","CAP_EDGE",EDGE,{"disambiguationData":[OSD([sQuery(id+"F18.wireOp",EDGE,"E26")])],"isStart":false});
            fillet(context, id + "F23", {"entities" : qUnion([Q0]), "radius" : 1 * mm, "tangentPropagation" : true, "allowEdgeOverflow" : false});
        }
        {
            var Q0;
            Q0=makeQuery(id+"F20.opExtrude","SWEPT_BODY",BODY,{"disambiguationData":[OSD([sQuery(id+"F18.wireOp",EDGE,"E26"),sQuery(id+"F18.wireOp",EDGE,"E27.trimOffspring")])]});
            var Q1;
            Q1=makeQuery(id+"F6.opExtrude","SWEPT_BODY",BODY,{"disambiguationData":[OSD([sQuery(id+"F0.wireOp",EDGE,"E1")])]});
            var Q2;
            Q2=makeQuery(id+"F9.opExtrude","SWEPT_BODY",BODY,{"disambiguationData":[OSD([sQuery(id+"F0.wireOp",EDGE,"E0")])]});
            var Q3;
            Q3=makeQuery(id+"F22.opExtrude","SWEPT_BODY",BODY,{"disambiguationData":[OSD([sQuery(id+"F18.wireOp",EDGE,"E26"),sQuery(id+"F18.wireOp",EDGE,"E27.trimOffspring")])]});
            var Q4;
            Q4=makeQuery(id+"F2.opExtrude","SWEPT_BODY",BODY,{"disambiguationData":[OSD([sQuery(id+"F0.wireOp",EDGE,"E5")])]});
            var Q5;
            Q5=makeQuery(id+"F1.opExtrude","SWEPT_BODY",BODY,{"disambiguationData":[OSD([sQuery(id+"F0.wireOp",EDGE,"E6"),sQuery(id+"F0.wireOp",EDGE,"E20")])]});
            var Q6;
            Q6=makeQuery(id+"F8.opExtrude","SWEPT_BODY",BODY,{"disambiguationData":[OSD([sQuery(id+"F0.wireOp",EDGE,"E0"),sQuery(id+"F0.wireOp",EDGE,"E1"),sQuery(id+"F0.wireOp",EDGE,"E2"),sQuery(id+"F0.wireOp",EDGE,"E3"),sQuery(id+"F0.wireOp",EDGE,"E4"),sQuery(id+"F0.wireOp",EDGE,"E5"),sQuery(id+"F0.wireOp",EDGE,"E6"),sQuery(id+"F0.wireOp",EDGE,"E7")])]});
            var Q7;
            Q7=makeQuery(id+"F4.opExtrude","SWEPT_BODY",BODY,{"disambiguationData":[OSD([sQuery(id+"F0.wireOp",EDGE,"E3")])]});
            var Q8;
            Q8=makeQuery(id+"F3.opExtrude","SWEPT_BODY",BODY,{"disambiguationData":[OSD([sQuery(id+"F0.wireOp",EDGE,"E4")])]});
            var Q9;
            Q9=makeQuery(id+"F5.opExtrude","SWEPT_BODY",BODY,{"disambiguationData":[OSD([sQuery(id+"F0.wireOp",EDGE,"E2")])]});
            var Q10;
            Q10=sQuery(id+"F0.wireOp",EDGE,"E20");
            transform(context, id + "F24", {"entities" : qUnion([Q0, Q1, Q2, Q3, Q4, Q5, Q6, Q7, Q8, Q9]), "transformType" : TransformType.ROTATION, "transformAxis" : qUnion([Q10]), "angle" : 85 * degree, "makeCopy" : false});
        }
        {
            var Q0;
            Q0=makeQuery(id+"F22.opExtrude","CAP_FACE",FACE,{"disambiguationData":[OSD([sQuery(id+"F18.wireOp",EDGE,"E26"),sQuery(id+"F18.wireOp",EDGE,"E27.trimOffspring")])],"isStart":false});
            var sketch = newSketch(context, id + "F25", { "sketchPlane" : qUnion([Q0])});
            skText(sketch, "E28", { "text": "Texturas", "fontName": "RobotoSlab-Bold.ttf"});
            skText(sketch, "E29", { "text": "Hilo", "fontName": "RobotoSlab-Bold.ttf"});
            skText(sketch, "E30", { "text": "Whatsapp: ", "fontName": "RobotoSlab-Bold.ttf"});
            skText(sketch, "E31", { "text": "5516776273", "fontName": "RobotoSlab-Bold.ttf"});
            const initialGuessF25  = {"E28": [0.00412, 0.04108, 1, 0, 0.00654], "E29": [0.0123, 0.0316, 1, 0, 0.00837], "E30": [0.00697, 0.02489, 1, 0, 0.00643], "E31": [0.00069, 0.0166, 1, 0, 0.007]};
            skSetInitialGuess(sketch, initialGuessF25);
            skSolve(sketch);
        }
        {
            var Q0;
            Q0 = qSketchRegion(id + "F25", true);
            extrude(context, id + "F26", {"entities" : qUnion([Q0]), "operationType" : NewBodyOperationType.REMOVE, "oppositeDirection" : true, "depth" : 1 * mm, "offsetDistance" : 25 * mm});
        }
        {
            var Q0;
            Q0=makeQuery(id+"F16.boolean.opBoolean","INTERSECT",EDGE,{"disambiguationData":[OD(1.0)],"derivedFrom":[makeQuery(id+"F6.opExtrude","CAP_FACE",FACE,{"disambiguationData":[OSD([sQuery(id+"F0.wireOp",EDGE,"E1")])],"isStart":false}),makeQuery(id+"F16.opExtrude","SWEPT_FACE",FACE,{"disambiguationData":[OSD([sQuery(id+"F0.wireOp",EDGE,"E25")])]})]});
            var Q1;
            Q1=makeQuery(id+"F16.boolean.opBoolean","INTERSECT",EDGE,{"disambiguationData":[OD(0.0)],"derivedFrom":[makeQuery(id+"F6.opExtrude","CAP_FACE",FACE,{"disambiguationData":[OSD([sQuery(id+"F0.wireOp",EDGE,"E1")])],"isStart":false}),makeQuery(id+"F16.opExtrude","SWEPT_FACE",FACE,{"disambiguationData":[OSD([sQuery(id+"F0.wireOp",EDGE,"E25")])]})]});
            var Q2;
            Q2=makeQuery(id+"F15.boolean.opBoolean","INTERSECT",EDGE,{"disambiguationData":[OD(1.0)],"derivedFrom":[makeQuery(id+"F5.opExtrude","CAP_FACE",FACE,{"disambiguationData":[OSD([sQuery(id+"F0.wireOp",EDGE,"E2")])],"isStart":false}),makeQuery(id+"F15.opExtrude","SWEPT_FACE",FACE,{"disambiguationData":[OSD([sQuery(id+"F0.wireOp",EDGE,"E24")])]})]});
            var Q3;
            Q3=makeQuery(id+"F15.boolean.opBoolean","INTERSECT",EDGE,{"disambiguationData":[OD(0.0)],"derivedFrom":[makeQuery(id+"F5.opExtrude","CAP_FACE",FACE,{"disambiguationData":[OSD([sQuery(id+"F0.wireOp",EDGE,"E2")])],"isStart":false}),makeQuery(id+"F15.opExtrude","SWEPT_FACE",FACE,{"disambiguationData":[OSD([sQuery(id+"F0.wireOp",EDGE,"E24")])]})]});
            var Q4;
            Q4=makeQuery(id+"F14.boolean.opBoolean","INTERSECT",EDGE,{"disambiguationData":[OD(0.0)],"derivedFrom":[makeQuery(id+"F4.opExtrude","CAP_FACE",FACE,{"disambiguationData":[OSD([sQuery(id+"F0.wireOp",EDGE,"E3")])],"isStart":false}),makeQuery(id+"F14.opExtrude","SWEPT_FACE",FACE,{"disambiguationData":[OSD([sQuery(id+"F0.wireOp",EDGE,"E23")])]})]});
            var Q5;
            Q5=makeQuery(id+"F14.boolean.opBoolean","INTERSECT",EDGE,{"disambiguationData":[OD(1.0)],"derivedFrom":[makeQuery(id+"F4.opExtrude","CAP_FACE",FACE,{"disambiguationData":[OSD([sQuery(id+"F0.wireOp",EDGE,"E3")])],"isStart":false}),makeQuery(id+"F14.opExtrude","SWEPT_FACE",FACE,{"disambiguationData":[OSD([sQuery(id+"F0.wireOp",EDGE,"E23")])]})]});
            var Q6;
            Q6=makeQuery(id+"F13.boolean.opBoolean","INTERSECT",EDGE,{"disambiguationData":[OD(0.0)],"derivedFrom":[makeQuery(id+"F3.opExtrude","CAP_FACE",FACE,{"disambiguationData":[OSD([sQuery(id+"F0.wireOp",EDGE,"E4")])],"isStart":false}),makeQuery(id+"F13.opExtrude","SWEPT_FACE",FACE,{"disambiguationData":[OSD([sQuery(id+"F0.wireOp",EDGE,"E22")])]})]});
            var Q7;
            Q7=makeQuery(id+"F13.boolean.opBoolean","INTERSECT",EDGE,{"disambiguationData":[OD(1.0)],"derivedFrom":[makeQuery(id+"F3.opExtrude","CAP_FACE",FACE,{"disambiguationData":[OSD([sQuery(id+"F0.wireOp",EDGE,"E4")])],"isStart":false}),makeQuery(id+"F13.opExtrude","SWEPT_FACE",FACE,{"disambiguationData":[OSD([sQuery(id+"F0.wireOp",EDGE,"E22")])]})]});
            var Q8;
            Q8=makeQuery(id+"F12.boolean.opBoolean","INTERSECT",EDGE,{"disambiguationData":[OD(0.0)],"derivedFrom":[makeQuery(id+"F2.opExtrude","CAP_FACE",FACE,{"disambiguationData":[OSD([sQuery(id+"F0.wireOp",EDGE,"E5")])],"isStart":false}),makeQuery(id+"F12.opExtrude","SWEPT_FACE",FACE,{"disambiguationData":[OSD([sQuery(id+"F0.wireOp",EDGE,"E21")])]})]});
            var Q9;
            Q9=makeQuery(id+"F12.boolean.opBoolean","INTERSECT",EDGE,{"disambiguationData":[OD(1.0)],"derivedFrom":[makeQuery(id+"F2.opExtrude","CAP_FACE",FACE,{"disambiguationData":[OSD([sQuery(id+"F0.wireOp",EDGE,"E5")])],"isStart":false}),makeQuery(id+"F12.opExtrude","SWEPT_FACE",FACE,{"disambiguationData":[OSD([sQuery(id+"F0.wireOp",EDGE,"E21")])]})]});
            var Q10;
            {var subQ0=sQuery(id+"F0.wireOp",EDGE,"E20");Q10=makeQuery(id+"F17.boolean.opBoolean","INTERSECT",EDGE,{"disambiguationData":[OD(0.0)],"derivedFrom":[makeQuery(id+"F1.opExtrude","CAP_FACE",FACE,{"disambiguationData":[OSD([sQuery(id+"F0.wireOp",EDGE,"E6"),subQ0])],"isStart":false}),makeQuery(id+"F17.opExtrude","SWEPT_FACE",FACE,{"disambiguationData":[OSD([subQ0])]})]});}
            var Q11;
            {var subQ0=sQuery(id+"F0.wireOp",EDGE,"E20");Q11=makeQuery(id+"F17.boolean.opBoolean","INTERSECT",EDGE,{"disambiguationData":[OD(1.0)],"derivedFrom":[makeQuery(id+"F1.opExtrude","CAP_FACE",FACE,{"disambiguationData":[OSD([sQuery(id+"F0.wireOp",EDGE,"E6"),subQ0])],"isStart":false}),makeQuery(id+"F17.opExtrude","SWEPT_FACE",FACE,{"disambiguationData":[OSD([subQ0])]})]});}
            fillet(context, id + "F27", {"entities" : qUnion([Q0, Q1, Q2, Q3, Q4, Q5, Q6, Q7, Q8, Q9, Q10, Q11]), "radius" : 5 * mm, "tangentPropagation" : true, "allowEdgeOverflow" : false});
        }
    });
